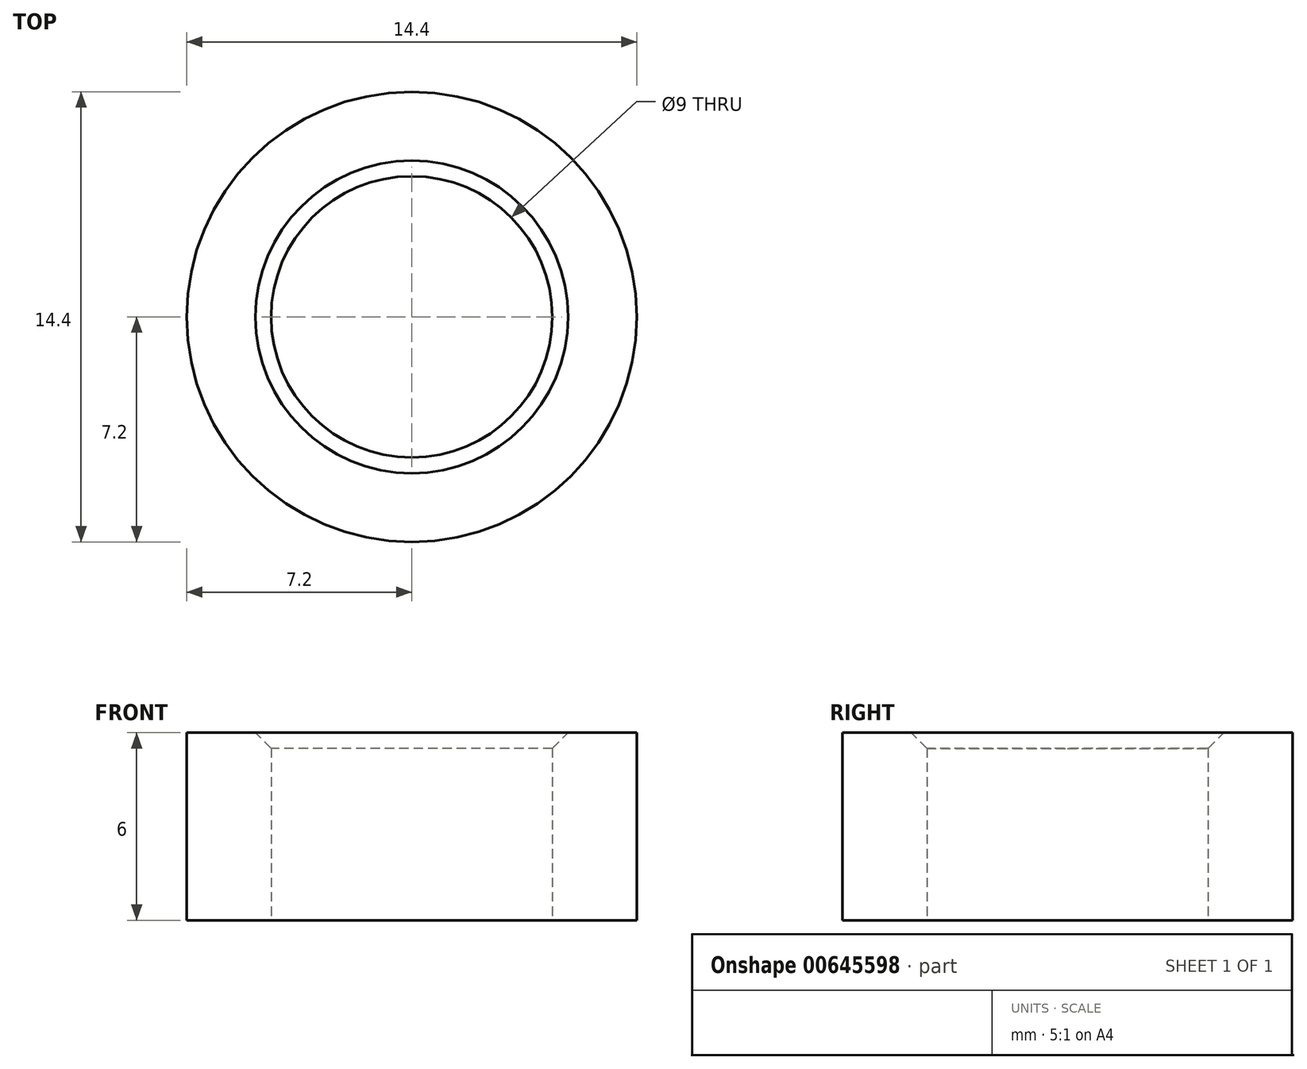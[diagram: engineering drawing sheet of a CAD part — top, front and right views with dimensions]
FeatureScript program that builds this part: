
annotation { "Feature Type Name" : "Feature", "Feature Type Description" : "" }
export const myFeature = defineFeature(function(context is Context, id is Id, definition is map)
    precondition{}
    {
        {
            var Q0;
            Q0=qCreatedBy(makeId("Top.planeOp"),FACE);
            var sketch = newSketch(context, id + "F0", { "sketchPlane" : qUnion([Q0])});
            skCircle(sketch, "E0", {"center": v(0, 0) * mm, "radius": 7.2 * mm});
            skCircle(sketch, "E1", {"center": v(0, 0) * mm, "radius": 4.5 * mm});
            skSolve(sketch);
        }
        {
            var Q0;
            Q0=makeQuery(id+"F0.imprint","IMPRINT",FACE,{"disambiguationData":[TD([[makeQuery(id+"F0.imprint","IMPRINT",EDGE,{"derivedFrom":sQuery(id+"F0.wireOp",EDGE,"E0")}),1.0]])]});
            var Q1;
            Q1=sQuery(id+"F0.wireOp",EDGE,"E0");
            var Q2;
            Q2=sQuery(id+"F0.wireOp",EDGE,"E1");
            extrude(context, id + "F1", {"entities" : qUnion([Q0]), "surfaceEntities" : qUnion([Q1, Q2]), "depth" : 6 * mm, "offsetDistance" : 25.4 * mm});
        }
        {
            var Q0;
            Q0=makeQuery(id+"F1.opExtrude","CAP_EDGE",EDGE,{"disambiguationData":[OSD([sQuery(id+"F0.wireOp",EDGE,"E1")])],"isStart":false});
            chamfer(context, id + "F2", {"entities" : qUnion([Q0]), "chamferType" : ChamferType.OFFSET_ANGLE, "width" : 0.5 * mm, "oppositeDirection" : false, "angle" : 45 * degree, "tangentPropagation" : true});
        }
    });
